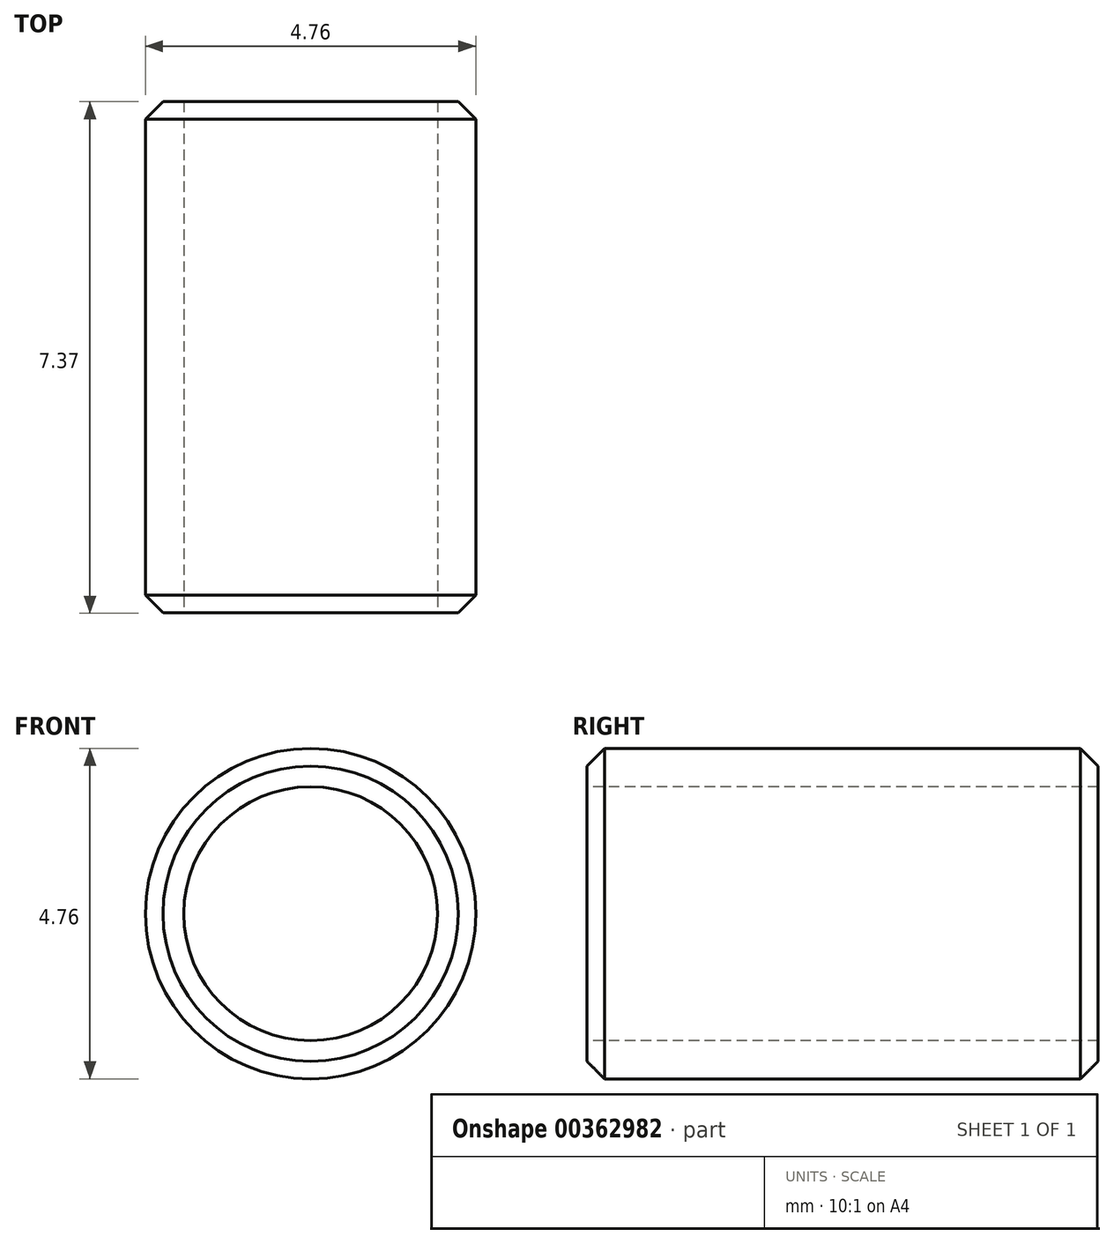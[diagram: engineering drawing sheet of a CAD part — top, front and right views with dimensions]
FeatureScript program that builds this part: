
annotation { "Feature Type Name" : "Feature", "Feature Type Description" : "" }
export const myFeature = defineFeature(function(context is Context, id is Id, definition is map)
    precondition{}
    {
        {
            var Q0;
            Q0=qCreatedBy(makeId("Front.planeOp"),FACE);
            var sketch = newSketch(context, id + "F0", { "sketchPlane" : qUnion([Q0])});
            skCircle(sketch, "E0", {"center": v(0, 0) * mm, "radius": 2.38 * mm});
            skSolve(sketch);
        }
        {
            var Q0;
            Q0=makeQuery(id+"F0.imprint","IMPRINT",FACE,{"disambiguationData":[TD([[makeQuery(id+"F0.imprint","IMPRINT",EDGE,{"derivedFrom":sQuery(id+"F0.wireOp",EDGE,"E0")}),1.0]])]});
            extrude(context, id + "F1", {"entities" : qUnion([Q0]), "depth" : 7.37 * mm});
        }
        {
            var Q0;
            Q0=makeQuery(id+"F1.opExtrude","CAP_FACE",FACE,{"disambiguationData":[OSD([sQuery(id+"F0.wireOp",EDGE,"E0")])],"isStart":false});
            var sketch = newSketch(context, id + "F2", { "sketchPlane" : qUnion([Q0])});
            skPoint(sketch, "E1", {"position": v(0, 0) * mm});
            skSolve(sketch);
        }
        {
            var Q0;
            Q0=sQuery(id+"F2.wireOp",VERTEX,"E1");
            var Q1;
            Q1=makeQuery(id+"F1.opExtrude","SWEPT_BODY",BODY,{"disambiguationData":[OSD([sQuery(id+"F0.wireOp",EDGE,"E0")])]});
            hole(context, id + "F3", {"style" : HoleStyle.SIMPLE, "endStyle" : HoleEndStyle.THROUGH, "standardTappedOrClearance" : lookupTablePath({ "standard" : "ANSI", "size" : "#27 (0.14)", "type" : "Drilled" }), "standardBlindInLast" : lookupTablePath({ "standard" : "ANSI", "size" : "#27", "type" : "Drilled" }), "holeDiameter" : 3.66 * mm, "tappedDepth" : 5.4 * mm, "tapClearance" : 3, "locations" : qUnion([Q0]), "scope" : qUnion([Q1])});
        }
        {
            var Q0;
            Q0=makeQuery(id+"F1.opExtrude","CAP_EDGE",EDGE,{"disambiguationData":[OSD([sQuery(id+"F0.wireOp",EDGE,"E0")])],"isStart":false});
            var Q1;
            Q1=makeQuery(id+"F1.opExtrude","CAP_EDGE",EDGE,{"disambiguationData":[OSD([sQuery(id+"F0.wireOp",EDGE,"E0")])],"isStart":true});
            chamfer(context, id + "F4", {"entities" : qUnion([Q0, Q1]), "chamferType" : ChamferType.OFFSET_ANGLE, "width" : 0.25 * mm, "oppositeDirection" : false, "angle" : 45 * degree, "tangentPropagation" : true});
        }
    });
